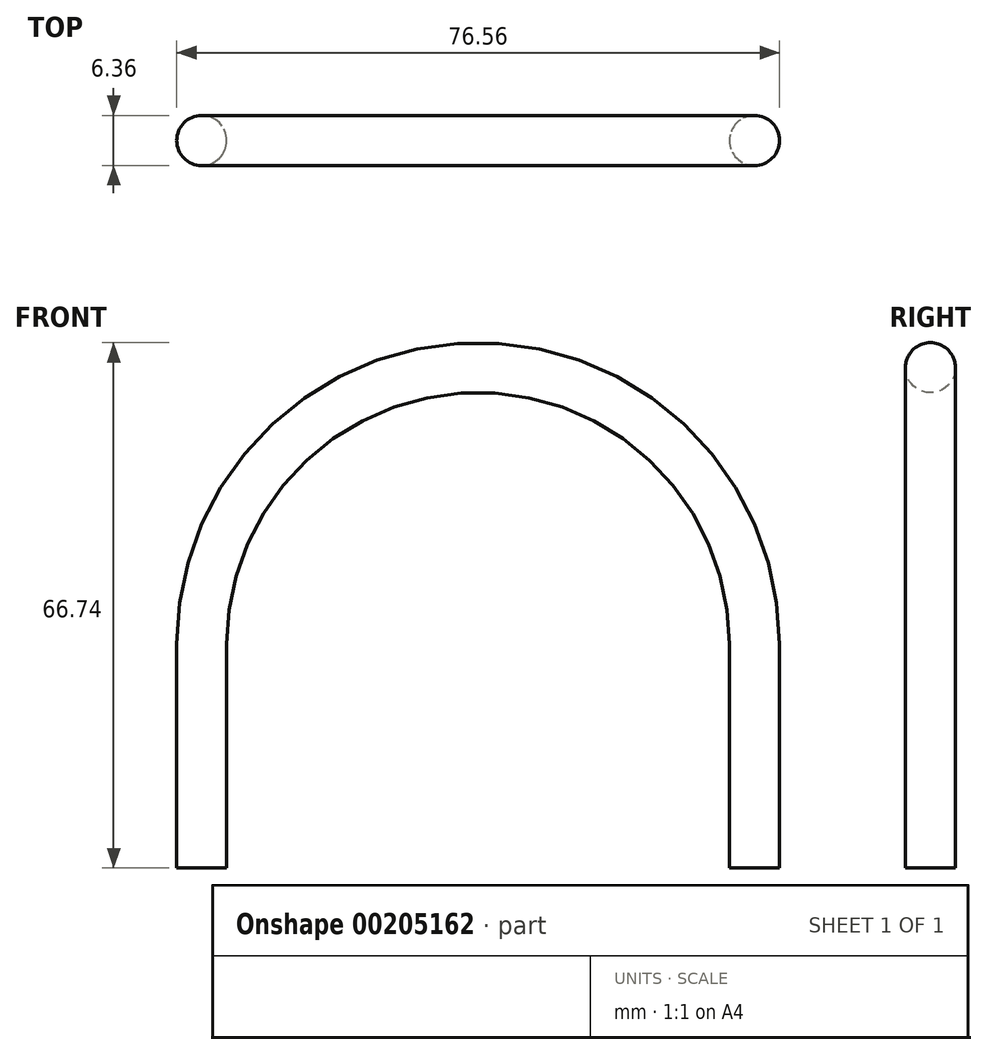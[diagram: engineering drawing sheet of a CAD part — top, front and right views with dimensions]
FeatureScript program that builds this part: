
annotation { "Feature Type Name" : "Feature", "Feature Type Description" : "" }
export const myFeature = defineFeature(function(context is Context, id is Id, definition is map)
    precondition{}
    {
        {
            var Q0;
            Q0=qCreatedBy(makeId("Front.planeOp"),FACE);
            var sketch = newSketch(context, id + "F0", { "sketchPlane" : qUnion([Q0])});
            skLineSegment(sketch, "E0", {"start": v(35.1, 0) * mm, "end": v(35.1, 28.46) * mm});
            skLineSegment(sketch, "E1", {"start": v(-35.1, 0) * mm, "end": v(-35.1, 28.46) * mm});
            skArc(sketch, "E2", {"start": v(35.1, 28.46) * mm, "mid": v(0, 63.56) * mm, "end": v(-35.1, 28.46) * mm});
            skSolve(sketch);
        }
        {
            var Q0;
            Q0=qCreatedBy(makeId("Top.planeOp"),FACE);
            var sketch = newSketch(context, id + "F1", { "sketchPlane" : qUnion([Q0])});
            skCircle(sketch, "E3", {"center": v(35.1, 0) * mm, "radius": 3.18 * mm});
            skSolve(sketch);
        }
        {
            var Q0;
            Q0=makeQuery(id+"F1.imprint","IMPRINT",FACE,{"disambiguationData":[TD([[makeQuery(id+"F1.imprint","IMPRINT",EDGE,{"derivedFrom":sQuery(id+"F1.wireOp",EDGE,"E3")}),1.0]])]});
            var Q1;
            Q1=sQuery(id+"F0.wireOp",EDGE,"E0");
            var Q2;
            Q2=sQuery(id+"F0.wireOp",EDGE,"E2");
            var Q3;
            Q3=sQuery(id+"F0.wireOp",EDGE,"E1");
            sweep(context, id + "F2", {"profiles" : qUnion([Q0]), "path" : qUnion([Q1, Q2, Q3])});
        }
    });
